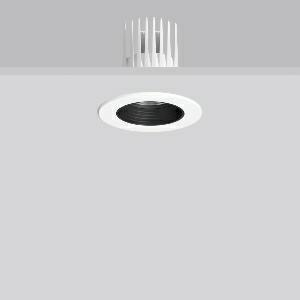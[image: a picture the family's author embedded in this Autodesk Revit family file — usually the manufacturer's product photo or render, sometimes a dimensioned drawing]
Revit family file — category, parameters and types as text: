
# Revit family: heledon_mini_e_901744_002_3_76_bc07
name_source: partatom
category: Lighting Fixtures
units: mm (PartAtom-declared; Revit-internal decimal feet)

## family parameters
Cut with Voids When Loaded = No
Host = Face
Light Source = No
Part Type = Normal
Room Calculation Point = No
Round Connector Dimension = Use Diameter
Shared = No

## types (1)
- HELEDON mini E (1 x LED Modul 935, 2150 lm, 3500)
    Apparent Load = 20 VA
    Approval mark = CE
    CIE Flux Codes = 96 100 100 100 100
    Color Rendering = 92
    Color Temperature = 3500
    Default Elevation = 1800 mm
    Description = Series: HELEDON mini
Round recessed downlight. Housing: die-cast aluminium, powder-coated. Black plastic ring and recessed LED to prevent glare from the side. Optical assembly with lens made of plastic (polycarbonate) for the best homogeneous light distribution - can be changed without tools. Best colour rendering index Ra>90. Suitable for Recessed ceiling mounting. Installation without tools thanks to spring fastening system. Including separate LED converter with connecting cable 600 mm.High quality converter without flickering and stroboscopic effect. Through-wiring box (5 pole) available as accessory. The following accessories can be mounted without use of tools: interchangeable lenses, decorative glasses, honeycomb louvre, clear and frosted diffusers, white interchangeable plastic ring. 
Colour: traffic white, matt (RAL 9016)
Diameter: 124 mm
Height: 3 mm
Cut-out diameter: 114 mm
Recess height: 170 mm
Luminaire: recess height: 120 mm
Lamp: LED
Socket: without socket
Colour temperature: 3500K
Colour rendering index (CRI): 92
System power: 20 W
Rated luminous flux: 2150 lm
Luminous efficiency: 108 lm/W
Control gear: Converter, dimmable, DALI
Protection class: II
Type of protection: IP 20
    Height = 0 mm  [stored 0 ft]
    Lamp = 1 x LED Modul 935
    Lamp Light Flux = 2150 lm
    Lamp count = 1
    Length = 124 mm  [stored 0.406824 ft]
    Lifetime = 50000 h
    Luminous efficacy = 108 lm/W
    Manufacturer = RZB
    ModVariant = No
    Model = 901744.002.3.76
    Mounting Place = Ceiling
    Mounting Type = Recessed
    Number of Poles = 1
    OnlyDefault = Yes
    Power Factor = 1
    Product Name = HELEDON mini E
    Product group = Recessed downlights
    ProductGroupID = 402
    Protection Class = Protection class II
    Protection Degree = IP 20
    RLX_Detail_Level = 1
    RLX_Emergency_Light_Flux = 0 lm
    RLX_Emergency_Type = 0
    RLX_Emergency_Type_DB = No
    RlxData = <blob elided: 122433 chars, md5=b0e8eb91>
    Socket = socket
    Standby Power = 0 W
    System Light Flux = 2150 lm
    System Power = 20 W
    Type Comments = Product without accessories
    Type Image = 901656.002.jpg
    URL = http://relux.com
    VarID = ---
    Voltage = 230 V
    Voltage Range = 220-240 V
    Weight = 0.00 kg
    Width = 0 mm  [stored 0 ft]

note: [stored X ft] marks values corroborated as IEEE doubles in the binary element streams (Revit-internal decimal feet)

## geometry (parser evidence)
native form markers: Blend x4, Sweep x12
no freeform markers — native parametric forms only
